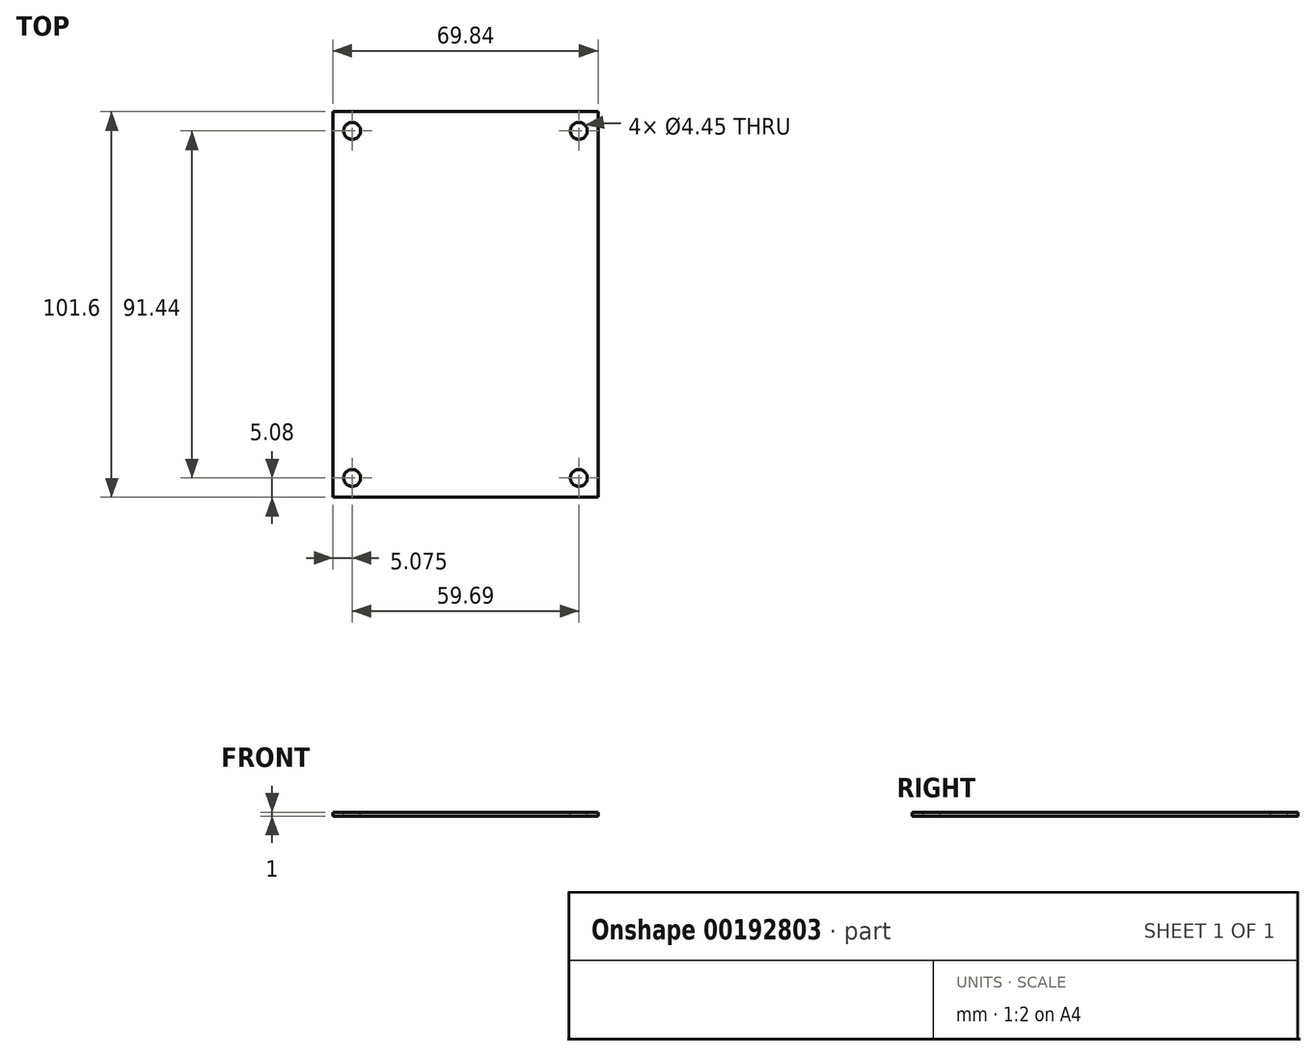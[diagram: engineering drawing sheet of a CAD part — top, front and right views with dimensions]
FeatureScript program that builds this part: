
annotation { "Feature Type Name" : "Feature", "Feature Type Description" : "" }
export const myFeature = defineFeature(function(context is Context, id is Id, definition is map)
    precondition{}
    {
        {
            var Q0;
            Q0=qCreatedBy(makeId("Top.planeOp"),FACE);
            var sketch = newSketch(context, id + "F0", { "sketchPlane" : qUnion([Q0])});
            skLineSegment(sketch, "E0.bottom", {"start": v(-34.92, 50.8) * mm, "end": v(34.93, 50.8) * mm});
            skLineSegment(sketch, "E0.top", {"start": v(-34.93, -50.8) * mm, "end": v(34.92, -50.8) * mm});
            skLineSegment(sketch, "E0.left", {"start": v(-34.92, 50.8) * mm, "end": v(-34.93, -50.8) * mm});
            skLineSegment(sketch, "E0.right", {"start": v(34.93, 50.8) * mm, "end": v(34.93, -50.8) * mm});
            skLineSegment(sketch, "E1", {"start": v(-34.92, 50.8) * mm, "end": v(34.92, -50.8) * mm, "construction": true});
            skSolve(sketch);
        }
        {
            var Q0;
            Q0=qSketchRegion(id+"F0",true);
            extrude(context, id + "F1", {"entities" : qUnion([Q0]), "depth" : 1 * mm});
        }
        {
            var Q0;
            Q0=makeQuery(id+"F1.opExtrude","CAP_FACE",FACE,{"disambiguationData":[OSD([sQuery(id+"F0.wireOp",EDGE,"E0.bottom"),sQuery(id+"F0.wireOp",EDGE,"E0.top"),sQuery(id+"F0.wireOp",EDGE,"E0.left"),sQuery(id+"F0.wireOp",EDGE,"E0.right")])],"isStart":false});
            var sketch = newSketch(context, id + "F2", { "sketchPlane" : qUnion([Q0])});
            skCircle(sketch, "E2", {"center": v(-29.85, 45.72) * mm, "radius": 2.22 * mm});
            skCircle(sketch, "E3", {"center": v(29.85, 45.72) * mm, "radius": 2.22 * mm});
            skCircle(sketch, "E4", {"center": v(-29.85, -45.72) * mm, "radius": 2.22 * mm});
            skCircle(sketch, "E5", {"center": v(29.85, -45.72) * mm, "radius": 2.22 * mm});
            skSolve(sketch);
        }
        {
            var Q0;
            Q0=qSketchRegion(id+"F2",true);
            extrude(context, id + "F3", {"entities" : qUnion([Q0]), "operationType" : NewBodyOperationType.REMOVE, "endBound" : BoundingType.THROUGH_ALL, "oppositeDirection" : true, "depth" : 25.4 * mm});
        }
    });
